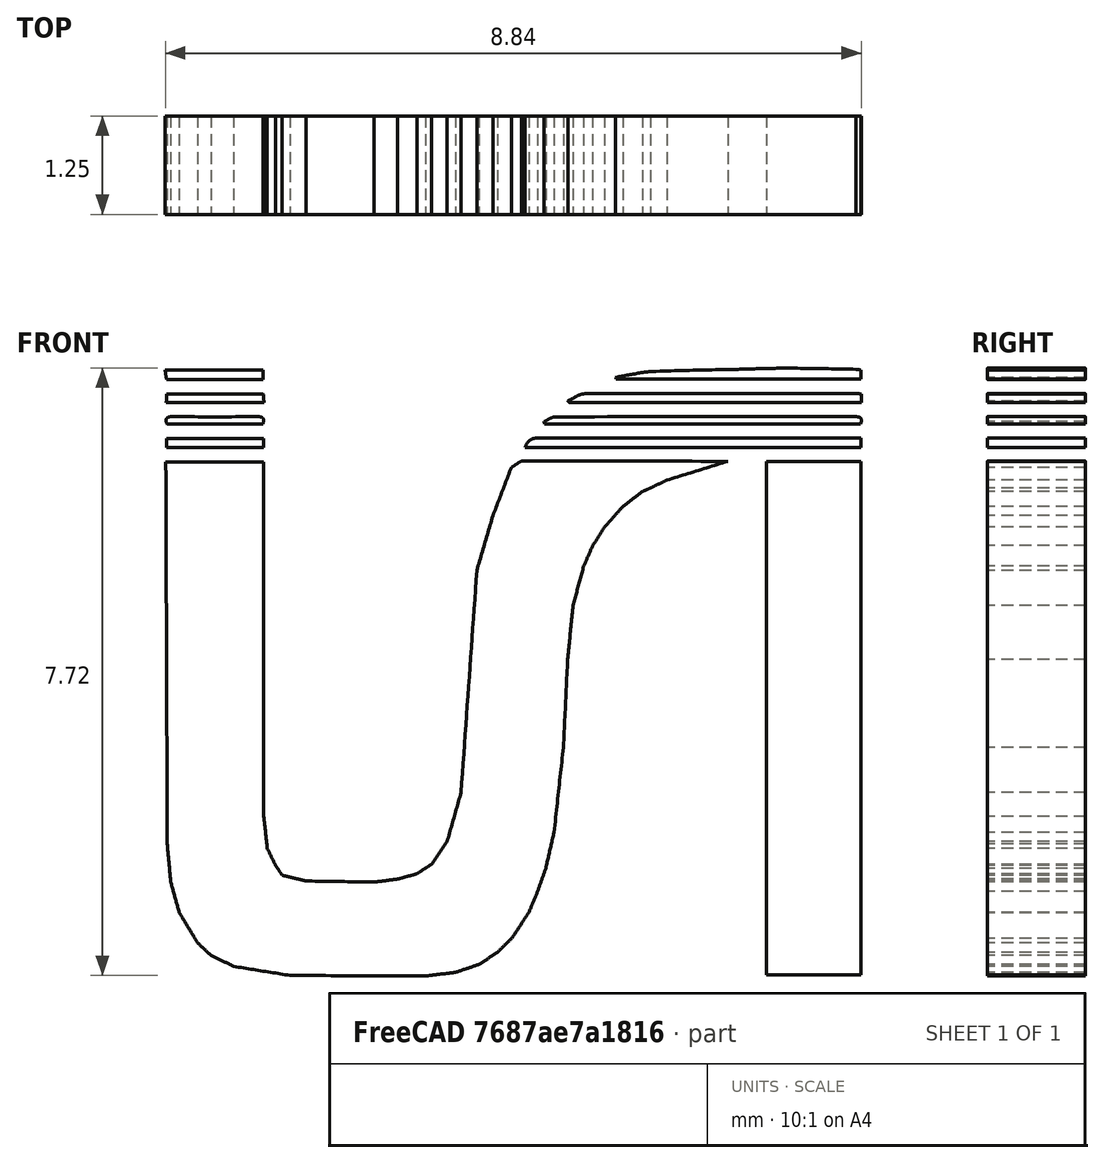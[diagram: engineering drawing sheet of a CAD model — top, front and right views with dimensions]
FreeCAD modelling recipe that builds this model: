
FCSTD DOCUMENT  (FreeCAD 0.16R6712 (Git))
Label: lsi
License: All rights reserved
LicenseURL: http://en.wikipedia.org/wiki/All_rights_reserved
objects: Part::Feature×11, Part::Extrusion×10, Mesh::Feature×1, Part::Part2DObjectPython×1, Part::MultiFuse×1, Part::FeaturePython×1, Part::Box×1, Part::Cut×1
note: 26 computed .brp shape members not serialized (recipe doc carries the construction recipe); baked Part::Feature solids carry a one-line shape summary decoded from their .brp

FEATURE [Mesh::Feature] Key_test6
FEATURE [Part::Feature] Key_test6001
  shape: bbox 57.89 x 5 x 19.55 mm, 706 faces, 0 solids (baked)
FEATURE [Part::Feature] Path001
  shape: bbox 11.99 x 65.22 x 2e-07 mm, 0 faces, 0 solids (baked)
FEATURE [Part::Feature] Path002
  shape: bbox 42.64 x 1.214 x 2e-07 mm, 0 faces, 0 solids (baked)
FEATURE [Part::Feature] Path003
  shape: bbox 37.25 x 1.173 x 2e-07 mm, 0 faces, 0 solids (baked)
FEATURE [Part::Feature] Path004
  shape: bbox 40.43 x 0.9313 x 2e-07 mm, 0 faces, 0 solids (baked)
FEATURE [Part::Feature] Path005
  shape: bbox 31.16 x 1.383 x 2e-07 mm, 0 faces, 0 solids (baked)
FEATURE [Part::Feature] Path006
  shape: bbox 12.47 x 1.185 x 2e-07 mm, 0 faces, 0 solids (baked)
FEATURE [Part::Feature] Path007
  shape: bbox 12.3 x 1.101 x 2e-07 mm, 0 faces, 0 solids (baked)
FEATURE [Part::Feature] Path008
  shape: bbox 12.42 x 1.101 x 2e-07 mm, 0 faces, 0 solids (baked)
FEATURE [Part::Feature] Path009
  shape: bbox 12.54 x 0.9313 x 2e-07 mm, 0 faces, 0 solids (baked)
FEATURE [Part::Extrusion] Extrude001
  Base = -> Path001
  Dir = (0,0,5)
  Solid = true
FEATURE [Part::Extrusion] Extrude002
  Base = -> Path002
  Dir = (0,0,5)
  Solid = true
FEATURE [Part::Extrusion] Extrude003
  Base = -> Path003
  Dir = (0,0,5)
  Solid = true
FEATURE [Part::Extrusion] Extrude004
  Base = -> Path004
  Dir = (0,0,5)
  Solid = true
FEATURE [Part::Extrusion] Extrude005
  Base = -> Path005
  Dir = (0,0,5)
  Solid = true
FEATURE [Part::Extrusion] Extrude006
  Base = -> Path006
  Dir = (0,0,5)
  Solid = true
FEATURE [Part::Extrusion] Extrude007
  Base = -> Path007
  Dir = (0,0,5)
  Solid = true
FEATURE [Part::Extrusion] Extrude008
  Base = -> Path008
  Dir = (0,0,5)
  Solid = true
FEATURE [Part::Extrusion] Extrude009
  Base = -> Path009
  Dir = (0,0,5)
  Solid = true
FEATURE [Part::Feature] Path
  shape: bbox 72.46 x 65.52 x 2e-07 mm, 0 faces, 0 solids (baked)
FEATURE [Part::Part2DObjectPython] DWire  # Draft 2D object (typed FeaturePython)
  ChamferSize = 0
  Closed = true
  End = (69.6385,-92.579,0)
  FilletRadius = 0
  Length = 341.588
  MakeFace = true
  Points = (44) [(69.4549,-44.0549,0),(81.8727,-44.0549,0),(81.9009,-89.0976,0),(82.3524,-93.1616,0),(83.3841,-95.2767,0),(84.2392,-96.5593,0),(87.293,-97.2922,0),+37 more]
  Start = (69.4549,-44.0549,0)
  Subdivisions = 0
FEATURE [Part::Extrusion] Extrude
  Base = -> DWire
  Dir = (0,0,5)
  Solid = true
FEATURE [Part::MultiFuse] Fusion
  Placement = pos=(0,0,0) rot=(1,0,0;1.5708rad)
  Shapes = -> [Extrude001,Extrude005,Extrude002,Extrude003,Extrude004,Extrude009,Extrude007,Extrude008,Extrude006,Extrude]
FEATURE [Part::FeaturePython] Clone  label="Clone of Fusion"  # Draft clone (typed FeaturePython)
  Objects = -> [Fusion]
  Placement = pos=(2,0.5,11.5) rot=(1,0,0;1.5708rad)
  Scale = (0.1,0.25,0.1)
FEATURE [Part::Box] Box  label="Cubo"
  Height = 24
  Length = 43
  Placement = pos=(29,-4,-3) rot=(0,0,1;0rad)
  Width = 26
FEATURE [Part::Cut] Cut
  Base = -> Key_test6001
  Tool = -> Box
